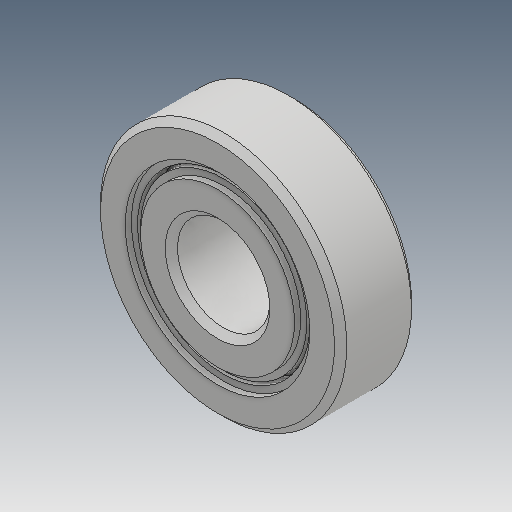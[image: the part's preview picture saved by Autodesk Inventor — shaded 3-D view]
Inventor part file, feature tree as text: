
AUTODESK INVENTOR PART (.ipt)
format: ipt  version: 2018 (Build 220112000, 112)  size: 845,824 bytes
history: native  units: mm
features: other x16, chamfer x2, revolve x1
ambient origin geometry x8: Origin, YZ Plane, XZ Plane, XY Plane, X Axis, Y Axis, Z Axis, Center Point
bodies: Volumenkörper1 (feature_tree), Volumenkörper2 (feature_tree), Volumenkörper3 (feature_tree), Volumenkörper4 (feature_tree), Volumenkörper5 (feature_tree), Volumenkörper6 (feature_tree), Volumenkörper7 (feature_tree), Volumenkörper8 (feature_tree), Volumenkörper9 (feature_tree), Volumenkörper10 (feature_tree), Volumenkörper11 (feature_tree), Volumenkörper12 (feature_tree), Volumenkörper13 (feature_tree), Volumenkörper14 (feature_tree), Volumenkörper15 (feature_tree), Volumenkörper16 (feature_tree), Volumenkörper17 (feature_tree), Volumenkörper18 (feature_tree), Volumenkörper19 (feature_tree)
feature tree (19):
  chamfer  "Chamfer2"  [1 undecoded]
  chamfer  "Chamfer1"  [1 undecoded]
  revolve  "Revolve2"  [1 undecoded]
  other  "CirPattern2[1]"
  other  "CirPattern2[2]"
  other  "CirPattern2[3]"
  other  "CirPattern2[4]"
  other  "CirPattern2[5]"
  other  "CirPattern2[6]"
  other  "CirPattern2[7]"
  other  "CirPattern2[8]"
  other  "CirPattern2[9]"
  other  "CirPattern2[10]"
  other  "CirPattern2[11]"
  other  "CirPattern2[12]"
  other  "CirPattern2[13]"
  other  "CirPattern2[14]"
  other  "CirPattern2[15]"
  other  "CirPattern2[16]"
note: 3 required parameter values undecoded (feature->parameter linkage not recoverable at this tier; creation-order binding heuristic only, values carry confidence <= 0.55)
